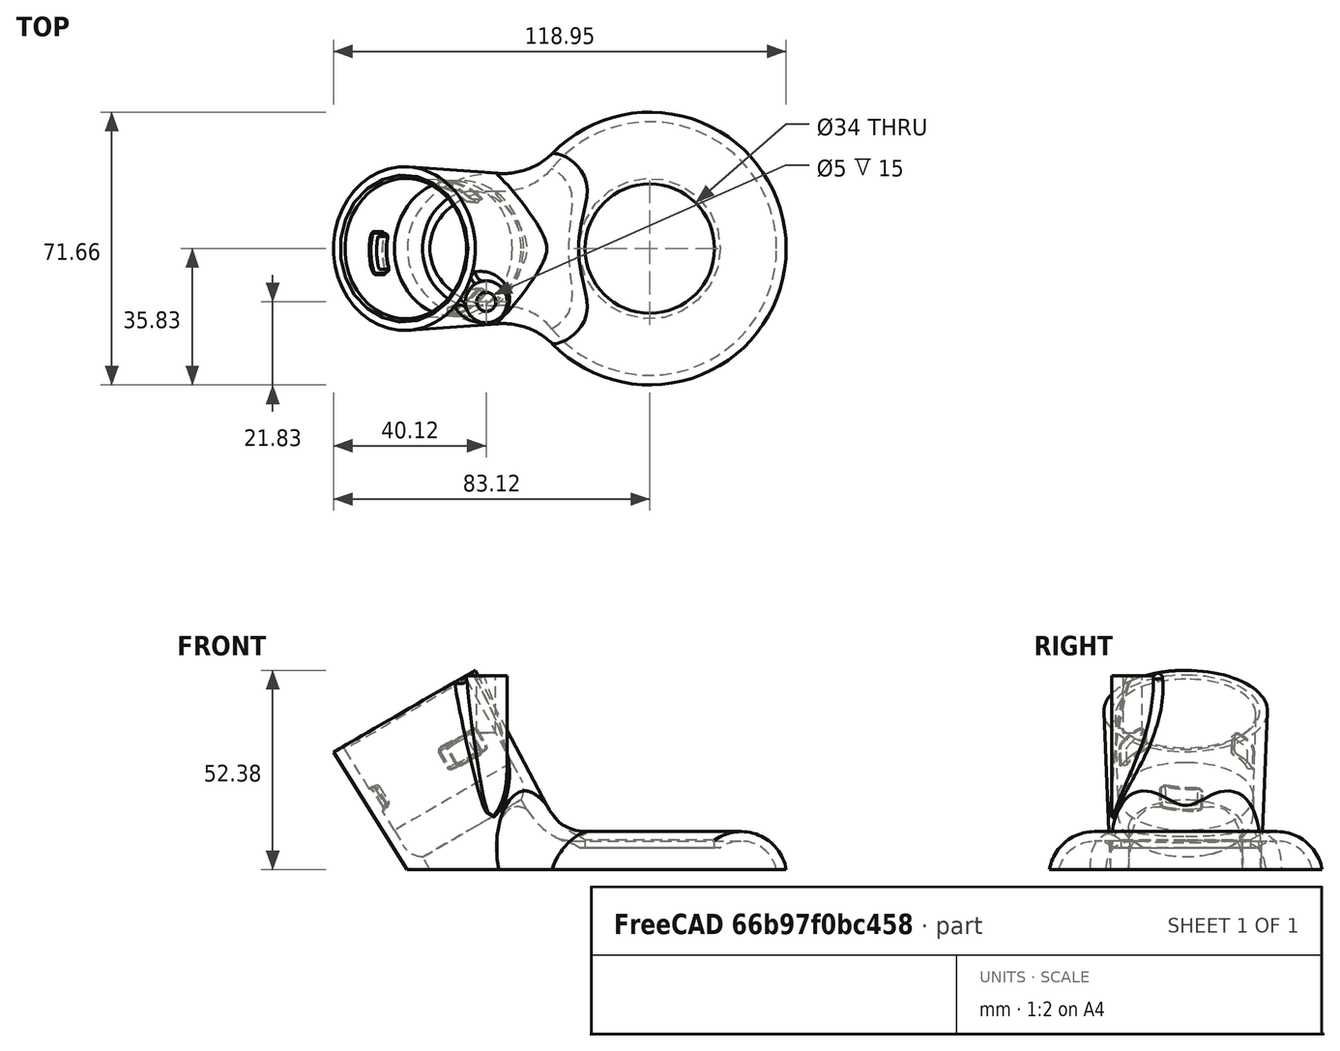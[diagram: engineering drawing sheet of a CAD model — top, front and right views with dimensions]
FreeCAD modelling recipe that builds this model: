
FCSTD DOCUMENT  (FreeCAD 0.20R)
Label: BoschHammerDrill_DustBoot
License: Creative Commons Attribution-NonCommercial
LicenseURL: http://creativecommons.org/licenses/by-nc/4.0/
objects: PartDesign::SubtractiveCylinder×3, PartDesign::Fillet×2, PartDesign::AdditiveTorus×1, PartDesign::AdditiveCone×1, PartDesign::SubtractiveBox×1, PartDesign::SubtractiveTorus×1, PartDesign::AdditiveCylinder×1, App::Link×1, PartDesign::Chamfer×1, PartDesign::Body×1, Part::Cut×1
note: 24 computed .brp shape members not serialized (recipe doc carries the construction recipe); baked Part::Feature solids carry a one-line shape summary decoded from their .brp
EXTERNAL_REF file=VacuumNozzle.FCStd obj=Body001

FEATURE [PartDesign::AdditiveTorus] Torus
  Angle1 = -180
  Angle2 = 180
  Angle3 = 360
  AttacherType = Attacher::AttachEngine3D
  MapMode = 5
  Radius1 = 24
  Radius2 = 12
  Refine = true
  Support = -> [XY_Plane]
FEATURE [PartDesign::SubtractiveCylinder] Cylinder
  Angle = 360
  AttacherType = Attacher::AttachEngine3D
  AttachmentOffset = pos=(0,0,-15) rot=(0,0,1;0rad)
  BaseFeature = -> Torus
  FirstAngle = 0
  Height = 30
  MapMode = 5
  Placement = pos=(0,0,-15) rot=(0,0,1;0rad)
  Radius = 17
  Refine = true
  SecondAngle = 0
  Support = -> [XY_Plane]
FEATURE [PartDesign::AdditiveCone] Cone
  Angle = 360
  AttacherType = Attacher::AttachEngine3D
  AttachmentOffset = pos=(-37,0,-4) rot=(0,-1,0;0.523599rad)
  BaseFeature = -> Cylinder
  Height = 55
  MapMode = 5
  Placement = pos=(-37,0,-4) rot=(0,-1,0;0.523599rad)
  Radius1 = 19.5
  Radius2 = 21.5
  Refine = true
  Support = -> [XY_Plane]
FEATURE [PartDesign::SubtractiveBox] Box
  AttacherType = Attacher::AttachEngine3D
  AttachmentOffset = pos=(-70,-40,-20) rot=(0,0,1;0rad)
  BaseFeature = -> Cone
  Height = 22
  Length = 110
  MapMode = 5
  Placement = pos=(-70,-40,-20) rot=(0,0,1;0rad)
  Refine = true
  Support = -> [XY_Plane]
  Width = 80
FEATURE [PartDesign::SubtractiveTorus] Torus001
  Angle1 = -180
  Angle2 = 180
  Angle3 = 360
  AttacherType = Attacher::AttachEngine3D
  BaseFeature = -> Box
  MapMode = 5
  Radius1 = 24
  Radius2 = 9.5
  Refine = true
  Support = -> [XY_Plane]
FEATURE [PartDesign::AdditiveCylinder] Cylinder002
  Angle = 360
  AttacherType = Attacher::AttachEngine3D
  AttachmentOffset = pos=(-43,-14,6) rot=(0,0,1;0rad)
  BaseFeature = -> Torus001
  FirstAngle = 0
  Height = 47
  MapMode = 5
  Placement = pos=(-43,-14,6) rot=(0,0,1;0rad)
  Radius = 5.5
  Refine = true
  SecondAngle = 0
  Support = -> [XY_Plane]
FEATURE [PartDesign::SubtractiveCylinder] Cylinder003
  Angle = 360
  AttacherType = Attacher::AttachEngine3D
  BaseFeature = -> Cylinder002
  FirstAngle = 0
  Height = 90
  MapMode = 11
  Placement = pos=(-64.5,0,43.6314) rot=(0.694747,-0.694747,0.186157;3.50969rad)
  Radius = 15
  Refine = true
  SecondAngle = 0
  Support = -> [Cylinder002]
FEATURE [App::Link] Link  label="NozzleKnockoutV2"
  LinkPlacement = pos=(-95.6847,3.69549e-07,97.45) rot=(0,1,0;1.0472rad)
  LinkedObject = -> <external VacuumNozzle.FCStd>#Body001
  Placement = pos=(-95.6847,3.69549e-07,97.45) rot=(0,1,0;1.0472rad)
FEATURE [PartDesign::SubtractiveCylinder] Cylinder004
  Angle = 360
  AttacherType = Attacher::AttachEngine3D
  BaseFeature = -> Cylinder003
  FirstAngle = 0
  Height = 15
  MapMode = 11
  Placement = pos=(-43,-14,53) rot=(-0.707107,0.707107,0;3.14159rad)
  Radius = 2.5
  Refine = true
  SecondAngle = 0
  Support = -> [Cylinder003]
FEATURE [PartDesign::Fillet] Fillet
  Base = -> Cylinder004 [Edge5,Edge18]
  BaseFeature = -> Cylinder004
  Placement = pos=(-43,-14,53) rot=(-0.707107,0.707107,0;3.14159rad)
  Radius = 19
  Refine = true
  SupportTransform = false
FEATURE [PartDesign::Fillet] Fillet001
  Base = -> Fillet [Edge23]
  BaseFeature = -> Fillet
  Placement = pos=(-43,-14,53) rot=(-0.707107,0.707107,0;3.14159rad)
  Radius = 2
  Refine = true
  SupportTransform = false
FEATURE [PartDesign::Chamfer] Chamfer
  Angle = 35
  Base = -> Fillet001 [Edge45]
  BaseFeature = -> Fillet001
  ChamferType = 2
  FlipDirection = false
  Placement = pos=(-43,-14,53) rot=(-0.707107,0.707107,0;3.14159rad)
  Refine = true
  Size = 2
  Size2 = 1
  SupportTransform = false
FEATURE [PartDesign::Body] Body  label="DustBoot_Blank"
  Group = -> [Torus,Cylinder,Cone,Box,Torus001,Cylinder002,Cylinder003,Cylinder004,Fillet,Fillet001,Chamfer]
  Origin = -> Origin
  Tip = -> Chamfer
FEATURE [Part::Cut] Cut  label="Bosch_HammerDrill_Dustboot"
  Base = -> Body
  Refine = true
  Tool = -> Link
